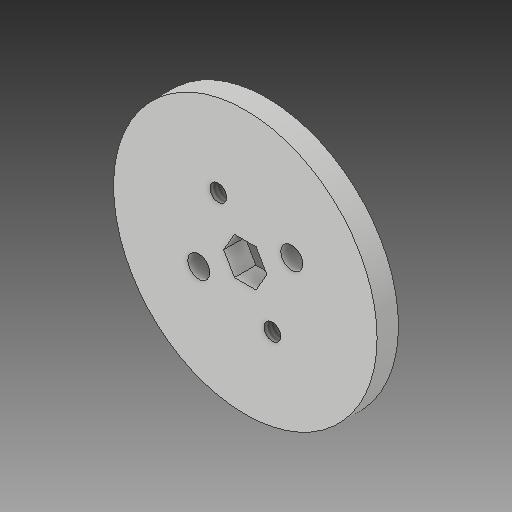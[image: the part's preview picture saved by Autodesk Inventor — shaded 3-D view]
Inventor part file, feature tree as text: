
AUTODESK INVENTOR PART (.ipt)
format: ipt  version: 2019 (Build 230136000, 136)  size: 240,640 bytes
history: native  units: in
note: dims shown in document units (in); Inventor stores cm internally (conversion verified against a paired STEP export)
features: sketch x9, thicken_offset x9, extrude x7, hole x2, pattern_circular x1
ambient origin geometry x8: Origin, YZ Plane, XZ Plane, XY Plane, X Axis, Y Axis, Z Axis, Center Point
bodies: Solid1 (feature_tree)
feature tree (28):
  extrude  "Extrusion1"  Depth=0.125in TaperAngle=0.0deg
  extrude  "Extrusion2"  TaperAngle=120.0deg  [1 undecoded]
  pattern_circular  "Circular Pattern1"  [2 undecoded]
  extrude  "Extrusion3"  Depth=0.125in
  sketch  "Sketch5"  dims[d7=0.3236in]
  extrude  "Extrusion4"  Depth=0.125in
  hole  "Hole2"  [1 undecoded]
  extrude  "Extrusion5"  Depth=0.125in TaperAngle=0.0deg
  extrude  "Extrusion6"  Depth=0.125in TaperAngle=360.0deg
  thicken_offset  "Thicken1"
  thicken_offset  "Thicken2"
  thicken_offset  "Thicken3"
  thicken_offset  "Thicken4"
  thicken_offset  "Thicken5"
  thicken_offset  "Thicken6"
  thicken_offset  "Thicken7"
  thicken_offset  "Thicken8"
  thicken_offset  "Thicken9"
  hole  "Hole5"  [1 undecoded]
  sketch  "Sketch15"  dims[d12=0.489in]
  extrude  "Extrusion9"  Depth=0.125in
  sketch  "Sketch1"  dims[d0=2.176in d1=0.125in d2=0.0in]
  sketch  "Sketch2"  dims[d3=120.0deg d5=120.0deg]
  sketch  "Sketch4"  dims[d6=120.0deg]
  sketch  "Sketch7"  dims[d8=0.2in]
  sketch  "Sketch8"  dims[d9=0.2in]
  sketch  "Sketch14"  dims[d11=0.7479in]
  sketch  "Sketch16"  dims[d13=0.323in d14=0.199in d15=0.199in d16=0.0423in d17=0.021in d18=0.125in d19=0.0in d20=1.1811in d21=360.0deg d49=1.0in d50=0.0in d51=0.02in d52=0.9375in d54=0.17in d55=0.9375in d57=0.17in d58=0.9375in d60=0.17in d61=0.9375in d63=0.17in d64=0.9375in d66=0.17in d67=1.0in d68=0.0in d69=0.9375in d70=0.938in d82=0.235in d86=0.4118in d88=0.935in d89=1.2386in d90=0.17in d91=0.75in d92=0.375in d93=0.25in d94=0.5635in d95=1.0in d96=0.8108in d105=0.205in d106=0.2077in d107=0.1287in d108=1.0in d109=0.0in d112=0.205in d113=0.1287in d114=1.0in d115=0.0in d116=0.025in d117=0.025in d118=0.025in d119=0.025in d120=0.025in d121=0.025in d122=0.025in d123=0.025in d124=0.025in d125=0.025in d126=0.025in d127=0.025in d128=0.015in d129=0.015in d130=0.015in d131=0.015in d132=0.015in d133=0.015in d170=0.315in d171=0.8252in d172=0.315in d173=0.4117in d174=0.098in d175=0.25in d176=0.375in d177=0.25in d178=0.5635in d179=0.375in d180=0.8108in d181=1.0in d182=0.0in]
note: 5 required parameter values undecoded (feature->parameter linkage not recoverable at this tier; creation-order binding heuristic only, values carry confidence <= 0.55)
